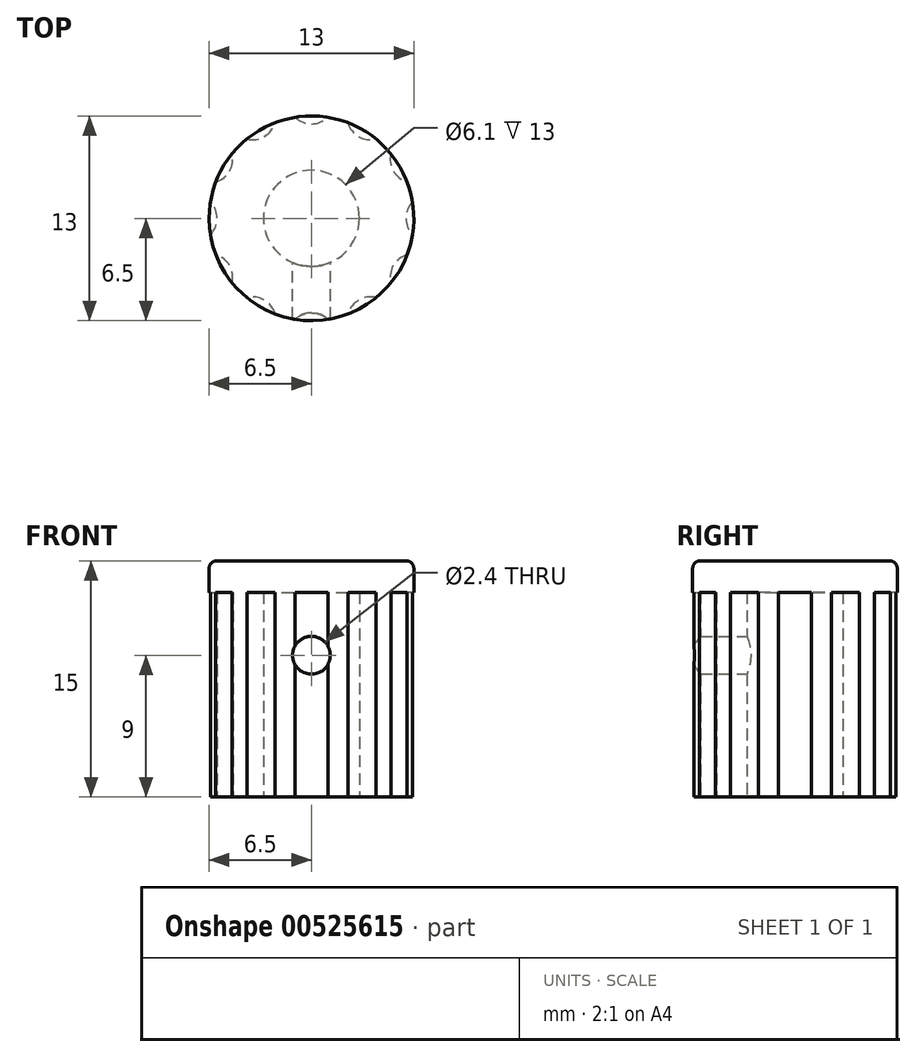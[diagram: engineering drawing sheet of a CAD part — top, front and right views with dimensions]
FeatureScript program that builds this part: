
annotation { "Feature Type Name" : "Feature", "Feature Type Description" : "" }
export const myFeature = defineFeature(function(context is Context, id is Id, definition is map)
    precondition{}
    {
        {
            var Q0;
            Q0=qCreatedBy(makeId("Front.planeOp"),FACE);
            var sketch = newSketch(context, id + "F0", { "sketchPlane" : qUnion([Q0])});
            skLineSegment(sketch, "E0", {"start": v(0, -2.23) * mm, "end": v(0, -5.1) * mm, "construction": true});
            skLineSegment(sketch, "E1", {"start": v(0, 0) * mm, "end": v(-5, 0) * mm});
            skLineSegment(sketch, "E2", {"start": v(-5, 0) * mm, "end": v(-5, 0) * mm});
            skLineSegment(sketch, "E3", {"start": v(-5, 0) * mm, "end": v(-6.5, 0) * mm});
            skLineSegment(sketch, "E4", {"start": v(-6.5, 0) * mm, "end": v(-6.5, 15) * mm});
            skLineSegment(sketch, "E5", {"start": v(-6.5, 15) * mm, "end": v(0, 15) * mm});
            skLineSegment(sketch, "E6", {"start": v(0, 0) * mm, "end": v(0, 15) * mm});
            skSolve(sketch);
        }
        {
            var Q0;
            Q0=qSketchRegion(id+"F0",true);
            var Q1;
            Q1=sQuery(id+"F0.wireOp",EDGE,"E0");
            revolve(context, id + "F1", {"entities" : qUnion([Q0]), "axis" : qUnion([Q1]), "revolveType" : RevolveType.FULL});
        }
        {
            var Q0;
            Q0=makeQuery(id+"F1.opRevolve","SWEPT_FACE",FACE,{"disambiguationData":[OSD([sQuery(id+"F0.wireOp",EDGE,"E1")])]});
            var sketch = newSketch(context, id + "F2", { "sketchPlane" : qUnion([Q0])});
            skCircle(sketch, "E7", {"center": v(0, 0) * mm, "radius": 3.05 * mm});
            skSolve(sketch);
        }
        {
            var Q0;
            Q0=qSketchRegion(id+"F2",true);
            extrude(context, id + "F3", {"entities" : qUnion([Q0]), "operationType" : NewBodyOperationType.REMOVE, "oppositeDirection" : true, "depth" : 13 * mm, "offsetDistance" : 25 * mm});
        }
        {
            var Q0;
            Q0=makeQuery(id+"F1.opRevolve","SWEPT_EDGE",EDGE,{"disambiguationData":[OSD([sQuery(id+"F0.wireOp",EDGE,"E4"),sQuery(id+"F0.wireOp",EDGE,"E5")])]});
            fillet(context, id + "F4", {"entities" : qUnion([Q0]), "radius" : 0.5 * mm, "tangentPropagation" : true, "allowEdgeOverflow" : false});
        }
        {
            var Q0;
            Q0=qCreatedBy(makeId("Front.planeOp"),FACE);
            var sketch = newSketch(context, id + "F5", { "sketchPlane" : qUnion([Q0])});
            skCircle(sketch, "E8", {"center": v(0, 9) * mm, "radius": 1.2 * mm});
            skSolve(sketch);
        }
        {
            var Q0;
            Q0=qSketchRegion(id+"F5",true);
            extrude(context, id + "F6", {"entities" : qUnion([Q0]), "operationType" : NewBodyOperationType.REMOVE, "depth" : 7 * mm, "offsetDistance" : 25 * mm});
        }
        {
            var Q0;
            Q0=makeQuery(id+"F1.opRevolve","SWEPT_FACE",FACE,{"disambiguationData":[OSD([sQuery(id+"F0.wireOp",EDGE,"E3")])]});
            var sketch = newSketch(context, id + "F7", { "sketchPlane" : qUnion([Q0])});
            skCircle(sketch, "E9", {"center": v(-7.5, 0) * mm, "radius": 1.5 * mm});
            skCircle(sketch, "E10.1.0", {"center": v(-6.5, -3.75) * mm, "radius": 1.5 * mm});
            skCircle(sketch, "E10.2.0", {"center": v(-3.75, -6.5) * mm, "radius": 1.5 * mm});
            skCircle(sketch, "E10.3.0", {"center": v(0, -7.5) * mm, "radius": 1.5 * mm});
            skCircle(sketch, "E10.4.0", {"center": v(3.75, -6.5) * mm, "radius": 1.5 * mm});
            skCircle(sketch, "E10.5.0", {"center": v(6.5, -3.75) * mm, "radius": 1.5 * mm});
            skCircle(sketch, "E10.6.0", {"center": v(7.5, 0) * mm, "radius": 1.5 * mm});
            skCircle(sketch, "E10.7.0", {"center": v(6.5, 3.75) * mm, "radius": 1.5 * mm});
            skCircle(sketch, "E10.8.0", {"center": v(3.75, 6.5) * mm, "radius": 1.5 * mm});
            skCircle(sketch, "E10.9.0", {"center": v(0, 7.5) * mm, "radius": 1.5 * mm});
            skCircle(sketch, "E10.10.0", {"center": v(-3.75, 6.5) * mm, "radius": 1.5 * mm});
            skCircle(sketch, "E10.11.0", {"center": v(-6.5, 3.75) * mm, "radius": 1.5 * mm});
            skPoint(sketch, "E10.center", {"position": v(0, 0) * mm});
            skSolve(sketch);
        }
        {
            var Q0;
            Q0=qSketchRegion(id+"F7",true);
            extrude(context, id + "F8", {"entities" : qUnion([Q0]), "operationType" : NewBodyOperationType.REMOVE, "oppositeDirection" : true, "depth" : 13 * mm, "offsetDistance" : 25 * mm});
        }
    });
